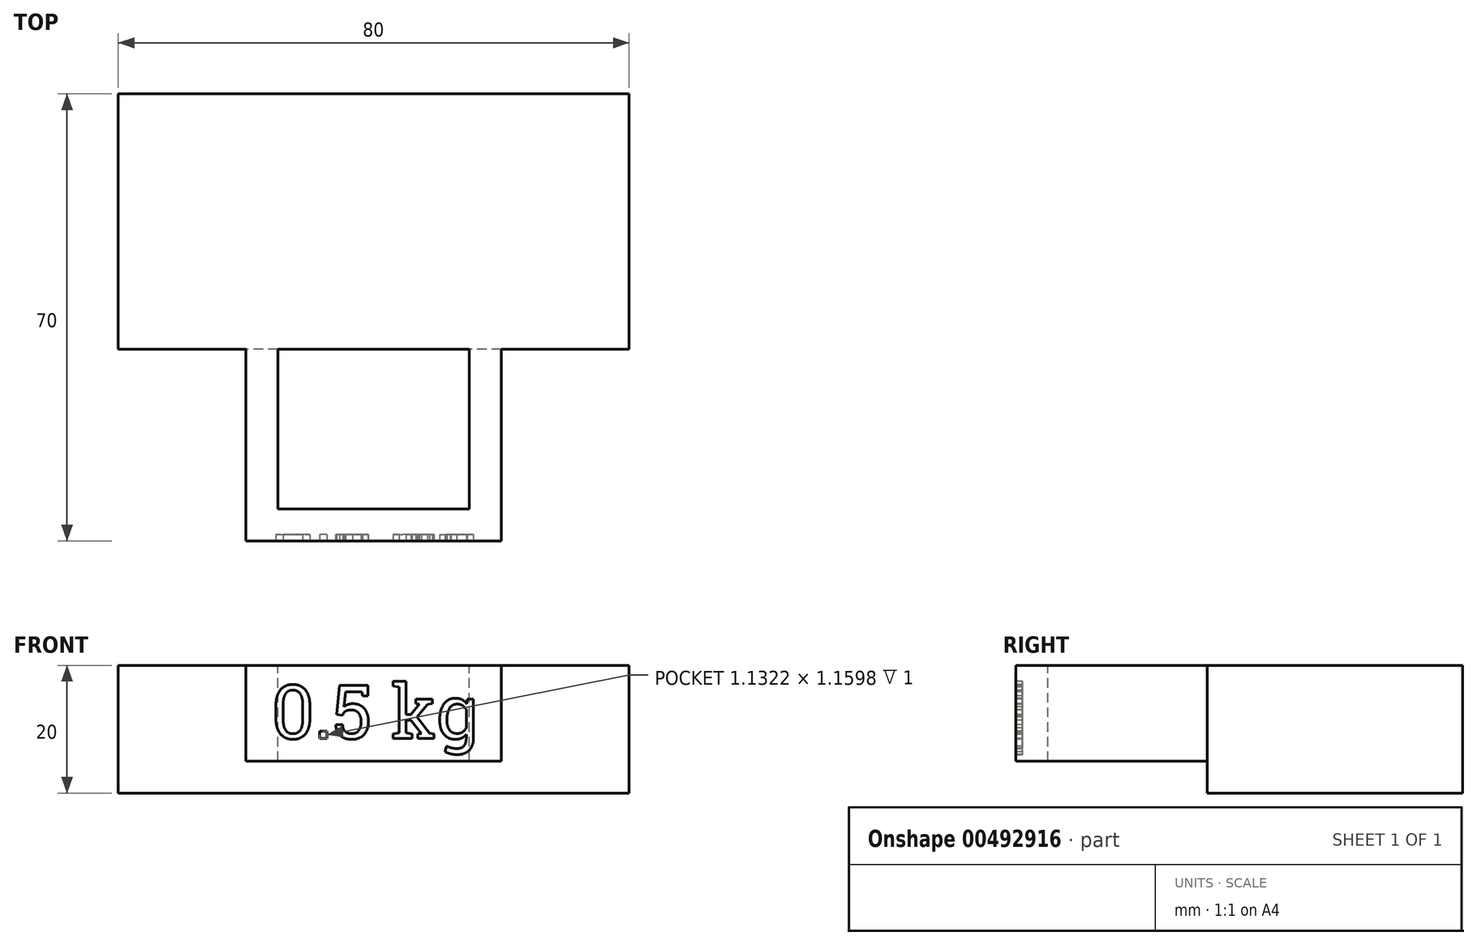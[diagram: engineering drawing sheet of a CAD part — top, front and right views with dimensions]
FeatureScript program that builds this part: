
annotation { "Feature Type Name" : "Feature", "Feature Type Description" : "" }
export const myFeature = defineFeature(function(context is Context, id is Id, definition is map)
    precondition{}
    {
        {
            var Q0;
            Q0=qCreatedBy(makeId("Top.planeOp"),FACE);
            var sketch = newSketch(context, id + "F0", { "sketchPlane" : qUnion([Q0])});
            skLineSegment(sketch, "E0.bottom", {"start": v(40, 20) * mm, "end": v(-40, 20) * mm});
            skLineSegment(sketch, "E0.top", {"start": v(40, -20) * mm, "end": v(-40, -20) * mm});
            skLineSegment(sketch, "E0.left", {"start": v(40, 20) * mm, "end": v(40, -20) * mm});
            skLineSegment(sketch, "E0.right", {"start": v(-40, 20) * mm, "end": v(-40, -20) * mm});
            skPoint(sketch, "E0.middle", {"position": v(0, 0) * mm});
            skSolve(sketch);
        }
        {
            var Q0;
            Q0=makeQuery(id+"F0.imprint","IMPRINT",FACE,{"disambiguationData":[TD([[makeQuery(id+"F0.imprint","IMPRINT",EDGE,{"derivedFrom":sQuery(id+"F0.wireOp",EDGE,"E0.bottom")}),1.0]])]});
            extrude(context, id + "F1", {"entities" : qUnion([Q0]), "depth" : 20 * mm});
        }
        {
            var Q0;
            Q0=makeQuery(id+"F1.opExtrude","CAP_FACE",FACE,{"disambiguationData":[OSD([sQuery(id+"F0.wireOp",EDGE,"E0.bottom"),sQuery(id+"F0.wireOp",EDGE,"E0.top"),sQuery(id+"F0.wireOp",EDGE,"E0.left"),sQuery(id+"F0.wireOp",EDGE,"E0.right")])],"isStart":false});
            var sketch = newSketch(context, id + "F2", { "sketchPlane" : qUnion([Q0])});
            skLineSegment(sketch, "E1.bottom", {"start": v(15, -45) * mm, "end": v(-15, -45) * mm});
            skLineSegment(sketch, "E1.top", {"start": v(15, 5) * mm, "end": v(-15, 5) * mm});
            skLineSegment(sketch, "E1.left", {"start": v(15, -45) * mm, "end": v(15, 5) * mm});
            skLineSegment(sketch, "E1.right", {"start": v(-15, -45) * mm, "end": v(-15, 5) * mm});
            skPoint(sketch, "E1.middle", {"position": v(0, -20) * mm});
            skLineSegment(sketch, "E2.bottom", {"start": v(20, -50) * mm, "end": v(-20, -50) * mm});
            skLineSegment(sketch, "E2.top", {"start": v(20, 10) * mm, "end": v(-20, 10) * mm});
            skLineSegment(sketch, "E2.left", {"start": v(20, -50) * mm, "end": v(20, 10) * mm});
            skLineSegment(sketch, "E2.right", {"start": v(-20, -50) * mm, "end": v(-20, 10) * mm});
            skSolve(sketch);
        }
        {
            var Q0;
            {var subQ7=sQuery(id+"F2.wireOp",EDGE,"E1.bottom");Q0=makeQuery(id+"F2.imprint","IMPRINT",FACE,{"disambiguationData":[TD([[makeQuery(id+"F2.imprint","IMPRINT",EDGE,{"derivedFrom":subQ7}),1.0]])]});}
            extrude(context, id + "F3", {"entities" : qUnion([Q0]), "operationType" : NewBodyOperationType.ADD, "oppositeDirection" : true, "depth" : 15 * mm});
        }
        {
            var Q0;
            Q0=makeQuery(id+"F3.opExtrude","SWEPT_FACE",FACE,{"disambiguationData":[OSD([sQuery(id+"F2.wireOp",EDGE,"E2.bottom")])]});
            var sketch = newSketch(context, id + "F4", { "sketchPlane" : qUnion([Q0])});
            skText(sketch, "E3", { "text": "0.5 kg", "fontName": "RobotoSlab-Regular.ttf"});
            const initialGuessF4  = {"E3": [-0.016, 0.00853, 1, 0, 0.00847]};
            skSetInitialGuess(sketch, initialGuessF4);
            skSolve(sketch);
        }
        {
            var Q0;
            Q0 = qSketchRegion(id + "F4", true);
            var Q1;
            Q1 = qConstructionFilter(qBodyType(qCreatedBy(id + "F4" ,EDGE), BodyType.WIRE), ConstructionObject.NO);
            extrude(context, id + "F5", {"entities" : qUnion([Q0]), "operationType" : NewBodyOperationType.REMOVE, "surfaceEntities" : qUnion([Q1]), "oppositeDirection" : true, "depth" : 1 * mm});
        }
    });
